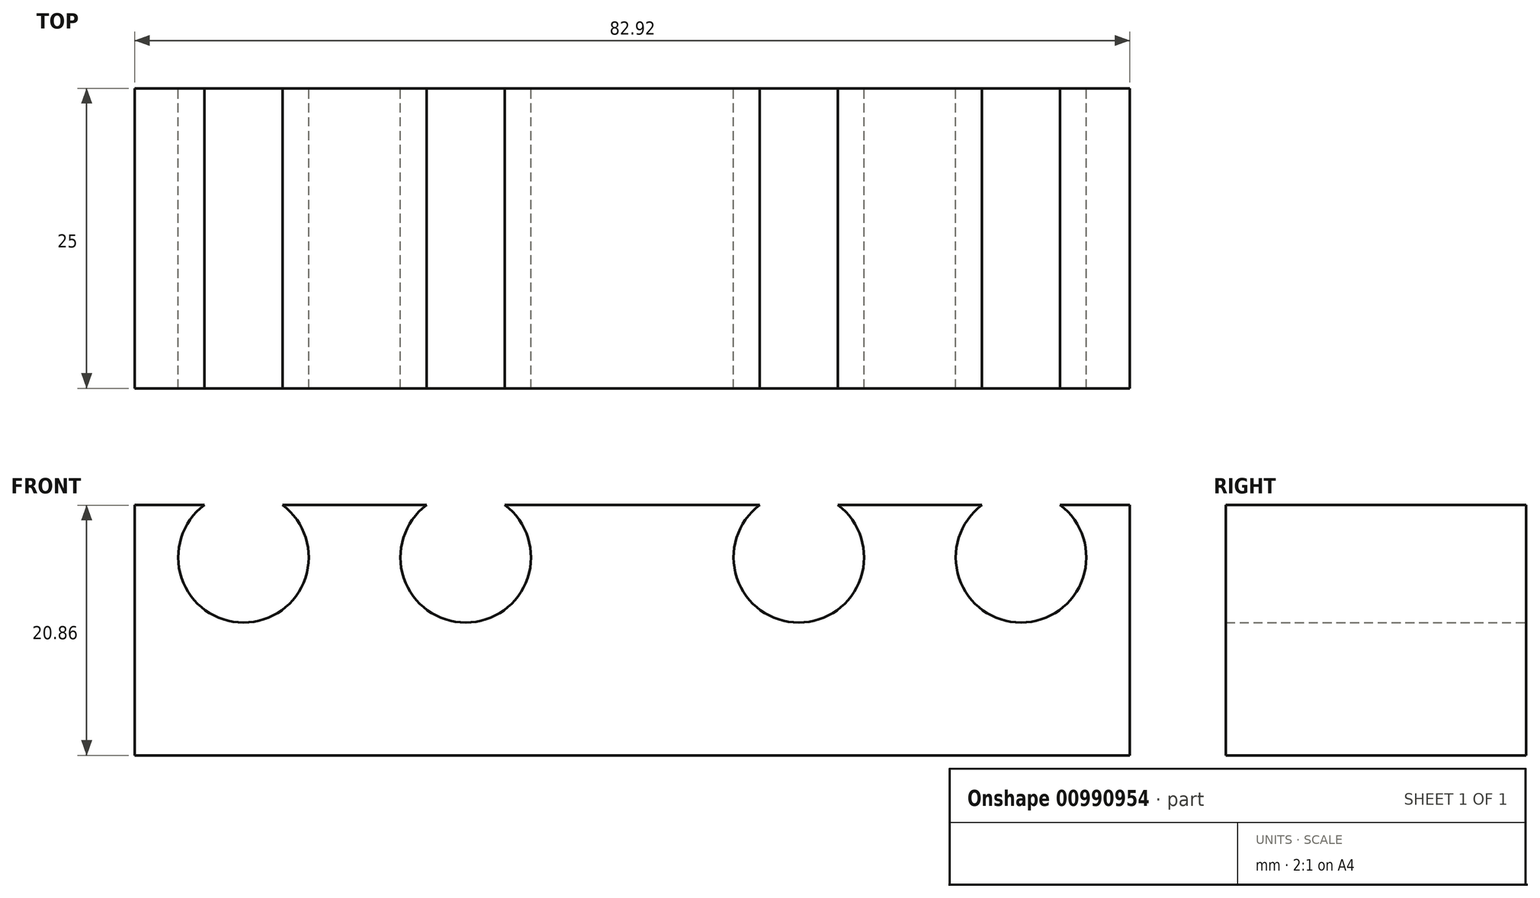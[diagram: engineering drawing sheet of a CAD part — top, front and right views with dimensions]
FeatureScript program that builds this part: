
annotation { "Feature Type Name" : "Feature", "Feature Type Description" : "" }
export const myFeature = defineFeature(function(context is Context, id is Id, definition is map)
    precondition{}
    {
        {
            var Q0;
            Q0=qCreatedBy(makeId("Front.planeOp"),FACE);
            var sketch = newSketch(context, id + "F0", { "sketchPlane" : qUnion([Q0])});
            skLineSegment(sketch, "E0.bottom", {"start": v(41.46, -10.43) * mm, "end": v(-41.46, -10.43) * mm});
            skLineSegment(sketch, "E0.top", {"start": v(41.46, 10.43) * mm, "end": v(-41.46, 10.43) * mm});
            skLineSegment(sketch, "E0.left", {"start": v(41.46, -10.43) * mm, "end": v(41.46, 10.43) * mm});
            skLineSegment(sketch, "E0.right", {"start": v(-41.46, -10.43) * mm, "end": v(-41.46, 10.43) * mm});
            skPoint(sketch, "E0.middle", {"position": v(0, 0) * mm});
            skLineSegment(sketch, "E1", {"start": v(0, 10.43) * mm, "end": v(0, -10.43) * mm, "construction": true});
            skCircle(sketch, "E2", {"center": v(-32.39, 6.08) * mm, "radius": 5.44 * mm});
            skCircle(sketch, "E3.MirrorC", {"center": v(-13.87, 6.08) * mm, "radius": 5.44 * mm});
            skCircle(sketch, "E4.MirrorC", {"center": v(13.87, 6.08) * mm, "radius": 5.44 * mm});
            skCircle(sketch, "E5.MirrorC", {"center": v(32.39, 6.08) * mm, "radius": 5.44 * mm});
            skSolve(sketch);
        }
        {
            var Q0;
            Q0=makeQuery(id+"F0.imprint","IMPRINT",FACE,{"disambiguationData":[TD([[makeQuery(id+"F0.imprint","IMPRINT",EDGE,{"derivedFrom":sQuery(id+"F0.wireOp",EDGE,"E0.bottom")}),-1.0]])]});
            extrude(context, id + "F1", {"entities" : qUnion([Q0]), "depth" : 25 * mm, "offsetDistance" : 25 * mm});
        }
    });
